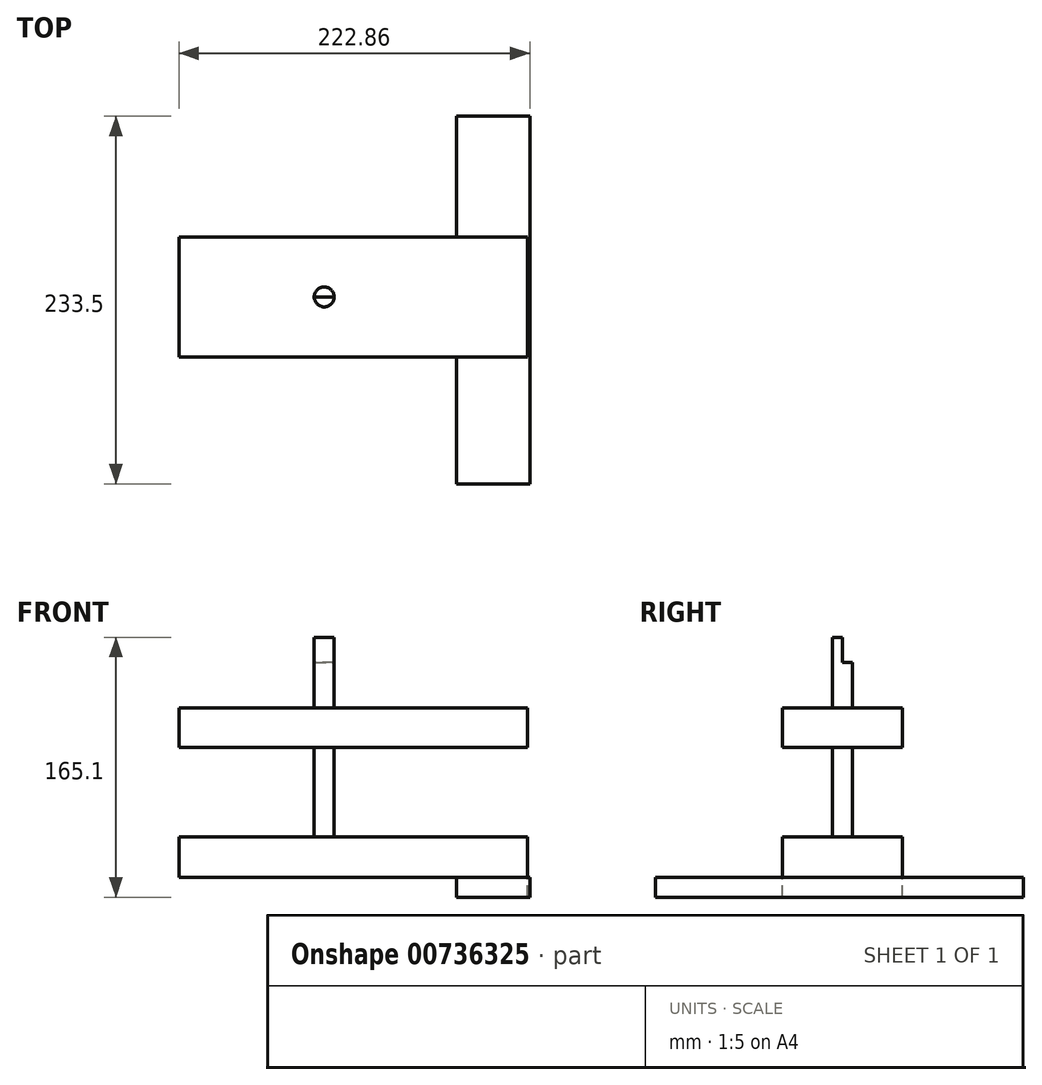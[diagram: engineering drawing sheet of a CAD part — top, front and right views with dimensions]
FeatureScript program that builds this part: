
annotation { "Feature Type Name" : "Feature", "Feature Type Description" : "" }
export const myFeature = defineFeature(function(context is Context, id is Id, definition is map)
    precondition{}
    {
        {
            var Q0;
            Q0=qCreatedBy(makeId("Top.planeOp"),FACE);
            var sketch = newSketch(context, id + "F0", { "sketchPlane" : qUnion([Q0])});
            skCircle(sketch, "E0", {"center": v(0, 0) * mm, "radius": 6.35 * mm});
            skSolve(sketch);
        }
        {
            var Q0;
            Q0=makeQuery(id+"F0.imprint","IMPRINT",FACE,{"disambiguationData":[TD([[makeQuery(id+"F0.imprint","IMPRINT",EDGE,{"derivedFrom":sQuery(id+"F0.wireOp",EDGE,"E0")}),1.0]])]});
            extrude(context, id + "F1", {"entities" : qUnion([Q0]), "depth" : 152.4 * mm, "offsetDistance" : 25.4 * mm});
        }
        {
            var Q0;
            Q0=qCreatedBy(makeId("Right.planeOp"),FACE);
            var sketch = newSketch(context, id + "F2", { "sketchPlane" : qUnion([Q0])});
            skLineSegment(sketch, "E1.bottom", {"start": v(12.7, 136.56) * mm, "end": v(0, 136.56) * mm});
            skLineSegment(sketch, "E1.top", {"start": v(12.7, 154.6) * mm, "end": v(0, 154.6) * mm});
            skLineSegment(sketch, "E1.left", {"start": v(12.7, 136.56) * mm, "end": v(12.7, 154.6) * mm});
            skLineSegment(sketch, "E1.right", {"start": v(0, 136.56) * mm, "end": v(0, 154.6) * mm});
            skSolve(sketch);
        }
        {
            var Q0;
            Q0 = qSketchRegion(id + "F2", true);
            extrude(context, id + "F3", {"entities" : qUnion([Q0]), "operationType" : NewBodyOperationType.REMOVE, "oppositeDirection" : true, "depth" : 25.4 * mm, "offsetDistance" : 25.4 * mm});
        }
        {
            var Q0;
            Q0 = qSketchRegion(id + "F2", true);
            extrude(context, id + "F4", {"entities" : qUnion([Q0]), "operationType" : NewBodyOperationType.REMOVE, "depth" : 25.4 * mm, "offsetDistance" : 25.4 * mm});
        }
        {
            var Q0;
            Q0=qCreatedBy(makeId("Front.planeOp"),FACE);
            var sketch = newSketch(context, id + "F5", { "sketchPlane" : qUnion([Q0])});
            skLineSegment(sketch, "E2.bottom", {"start": v(129.23, 82.62) * mm, "end": v(-92.3, 82.62) * mm});
            skLineSegment(sketch, "E2.top", {"start": v(129.23, 107.44) * mm, "end": v(-92.3, 107.44) * mm});
            skLineSegment(sketch, "E2.left", {"start": v(129.23, 82.62) * mm, "end": v(129.23, 107.44) * mm});
            skLineSegment(sketch, "E2.right", {"start": v(-92.3, 82.62) * mm, "end": v(-92.3, 107.44) * mm});
            skPoint(sketch, "E3.oppositeSnap0", {"position": v(-92.3, 95.03) * mm});
            skLineSegment(sketch, "E3.bottom", {"start": v(129.23, 0) * mm, "end": v(-92.3, 0) * mm});
            skLineSegment(sketch, "E3.top", {"start": v(129.23, 25.72) * mm, "end": v(-92.3, 25.72) * mm});
            skLineSegment(sketch, "E3.left", {"start": v(129.23, 0) * mm, "end": v(129.23, 25.72) * mm});
            skLineSegment(sketch, "E3.right", {"start": v(-92.3, 0) * mm, "end": v(-92.3, 25.72) * mm});
            skSolve(sketch);
        }
        {
            var Q0;
            Q0=makeQuery(id+"F5.imprint","IMPRINT",FACE,{"disambiguationData":[TD([[makeQuery(id+"F5.imprint","IMPRINT",EDGE,{"derivedFrom":sQuery(id+"F5.wireOp",EDGE,"E2.bottom")}),-1.0]])]});
            var Q1;
            Q1=makeQuery(id+"F5.imprint","IMPRINT",FACE,{"disambiguationData":[TD([[makeQuery(id+"F5.imprint","IMPRINT",EDGE,{"derivedFrom":sQuery(id+"F5.wireOp",EDGE,"E3.bottom")}),-1.0]])]});
            extrude(context, id + "F6", {"entities" : qUnion([Q0, Q1]), "operationType" : NewBodyOperationType.ADD, "depth" : 38.1 * mm, "offsetDistance" : 25.4 * mm});
        }
        {
            var Q0;
            Q0 = qSketchRegion(id + "F5", true);
            extrude(context, id + "F7", {"entities" : qUnion([Q0]), "operationType" : NewBodyOperationType.ADD, "oppositeDirection" : true, "depth" : 38.1 * mm, "offsetDistance" : 25.4 * mm});
        }
        {
            var Q0;
            {var subQ0=sQuery(id+"F5.wireOp",EDGE,"E3.bottom");Q0=makeQuery(id+"F7.boolean.opBoolean","MERGE",FACE,{"derivedFrom":[makeQuery(id+"F6.boolean.opBoolean","MERGE",FACE,{"derivedFrom":[makeQuery(id+"F1.opExtrude","CAP_FACE",FACE,{"disambiguationData":[OSD([sQuery(id+"F0.wireOp",EDGE,"E0")])],"isStart":true}),makeQuery(id+"F6.opExtrude","SWEPT_FACE",FACE,{"disambiguationData":[OSD([subQ0])]})]}),makeQuery(id+"F7.opExtrude","SWEPT_FACE",FACE,{"disambiguationData":[OSD([subQ0])]})]});}
            var sketch = newSketch(context, id + "F8", { "sketchPlane" : qUnion([Q0])});
            skLineSegment(sketch, "E4.bottom", {"start": v(130.55, -114.76) * mm, "end": v(83.99, -114.76) * mm});
            skLineSegment(sketch, "E4.top", {"start": v(130.55, 118.74) * mm, "end": v(83.99, 118.74) * mm});
            skLineSegment(sketch, "E4.left", {"start": v(130.55, -114.76) * mm, "end": v(130.55, 118.74) * mm});
            skLineSegment(sketch, "E4.right", {"start": v(83.99, -114.76) * mm, "end": v(83.99, 118.74) * mm});
            skSolve(sketch);
        }
        {
            var Q0;
            {var subQ1=sQuery(id+"F8.wireOp",EDGE,"E4.bottom");Q0=makeQuery(id+"F8.imprint","IMPRINT",FACE,{"disambiguationData":[TD([[makeQuery(id+"F8.imprint","IMPRINT",EDGE,{"derivedFrom":subQ1}),-1.0]])]});}
            extrude(context, id + "F9", {"entities" : qUnion([Q0]), "depth" : 12.7 * mm, "offsetDistance" : 25.4 * mm});
        }
    });
